# Revit family: PX602WL
name_source: partatom
category: Generic Models
revit_build: Autodesk Revit Architecture 2012 (Build: 20110309_2315(x64)
units: mm (PartAtom-declared; Revit-internal decimal feet)

## types (1)
- PX602WL
    * = Lens does not ship with projector
    Description = Professional Installation Projectors
    Dimensions (WxDxH) = 19.1 x 22.6 x 8.5in / 484 x 575 x 217mm
    Environmental - Humidity = 20-80% non-condensing
    Environmental - Operating Temperature = 41deg - 104degF / 5deg - 40degC
    Environmental - Storage = -14deg - 122degF / -10deg - 50degC
    Fan Noise = 39 dB normal / 34 dB eco
    Input Current = 6.6 - 2.5A
    Installation Orientation = Floor/Front, Floor/Rear, Ceiling/Front, Ceiling/Rear
    Manufacturer = NEC Display Solutions
    Model = PX602WL
    Net Weight = 40.8 lbs / 18.5 kg
    Optical - Contrast Ratio (up to) = 10,000 : 1 with auto iris
    Optical - Display /Technology = 0.65in DMD
    Optical - Keystone Correction = +/- 40deg horizontal, +/- 40deg vertical
    Optical - Laser Life (up to) = 2000 hours
    Optical - Lens* F-number, f-number NP33ZL = TBD
    Optical - Lens* F-number, f-number NP34ZL = F=2.3 to 2.57, f= 14.03 to 17.95mm
    Optical - Lens* F-number, f-number NP35ZL = F=2.0 to 2.32, f= 18.07 to 22.59mm
    Optical - Lens* F-number, f-number NP36ZL = F=2.0 to 2.32, f= 18.07 to 22.59mm
    Optical - Lens* F-number, f-number NP37ZL = F=2.3 to 3.39, f= 22.56 to 42.87mm
    Optical - Lens* F-number, f-number NP38ZL = TBD
    Optical - Lens* Focus = Powered
    Optical - Lens* Shift = Powered +/- 0.3 vertical, +/- 0.15 horizontal
    Optical - Lens* Zoom = Variable
    Optical - Lens* Zoom Ratio = Powered
    Optical - Light Output (lumens) = 6000 Normal / Eco = variable
    Optical - Projection Angle = 5.8 - 14.4deg tele / 10.9 - 18.4deg wide
    Optical - Projection Distance = 3.3 to 65.5ft / 1.01 to 19.96m
    Optical - Resolution Maximum = 4K 4096 x 2160
    Optical - Resolution Native = WUXGA 1280 x 800
    Optical - Screen Size (diagonal) = 50 to 300 in. / 1.27 to 7.62m
    Optical - Throw Area NP33ZL = 0.75 - 0.95 : 1
    Optical - Throw Area NP34ZL = 0.95 - 1.2 : 1
    Optical - Throw Area NP35ZL = 1.23 - 1.52 : 1
    Optical - Throw Area NP36FL = 1.28 - 1.6 : 1
    Optical - Throw Area NP37ZL = 1.52 - 2.92 : 1
    Optical - Throw Area NP38ZL = 2.9 - 5.5 : 1
    Optional Lenses = NP33ZL, NP34ZL, NP35ZL, NP36ZL, NP37ZL, NP38ZL
    Power Consumption (ECO off/ECO Mode/Standby/Standby-Power Saving = 590W / 460W / 6W / 0.5W
    Power Requirements = 100 - 240V AC, 50/60Hz
    Regulations = USA: UL 1950 FCC Class B, Canada: CSA950 (C-UL), NOM
    Signal Compatibility/Connectivity - 3D Sync Line = 3Pin D
    Signal Compatibility/Connectivity - External Control = RS-232, IR, HDBaseT, Wired LAN, DDC/CI, USB
    Signal Compatibility/Connectivity - Input/Output Terminals Monitor Out = HDMI
    Signal Compatibility/Connectivity - Input/Output Terminals Option Slot = OPS Option Slot
    Signal Compatibility/Connectivity - Input/Output Terminals RGB1 (analog) = VGA 15-pin D-sub
    Signal Compatibility/Connectivity - Input/Output Terminals RGB2 (analog) = 5 BNC
    Signal Compatibility/Connectivity - Input/Output Terminals RGB3 (digital) = HDMI w/ HDCP
    Signal Compatibility/Connectivity - Input/Output Terminals RGB4 (digital) = DisplayPort w/ HDCP
    Signal Compatibility/Connectivity - Input/Output Terminals RGB5 (digital) = HDBaseT
    Signal Compatibility/Connectivity - Macintosh Compatibility = Yes
    Signal Compatibility/Connectivity - Networking = HDBaseT, RJ-45
    Signal Compatibility/Connectivity - PC Signal Compatibility = VGA, SVGA, XGA, SXGA, SXGA+, UXGA, WUXGA, WXGA, FHD, 2K, QXGA, WQXGA, 4K
    Signal Compatibility/Connectivity - SD/HD Video Signal Compatibility = 480i, 480p, 576i, 576p, 720p, 1080i, 1080p
    Signal Compatibility/Connectivity - Scan Rate, Horizontal = 15 - 108 kHz
    Signal Compatibility/Connectivity - Scan Rate, Vertical = 48 - 120 Hz
    Signal Compatibility/Connectivity - Supported Video Standards = NTSC, NTSC4.43, PAL, PAL-60, PAL-M, PAL-N, SECAM
    Signal Compatibility/Connectivity - Sync Compatibility = Separate Sync /Composite Sync / Sync on G
    URL = www.necdisplay.com

## geometry (parser evidence)
native form markers: Sweep x2
no freeform markers — native parametric forms only
